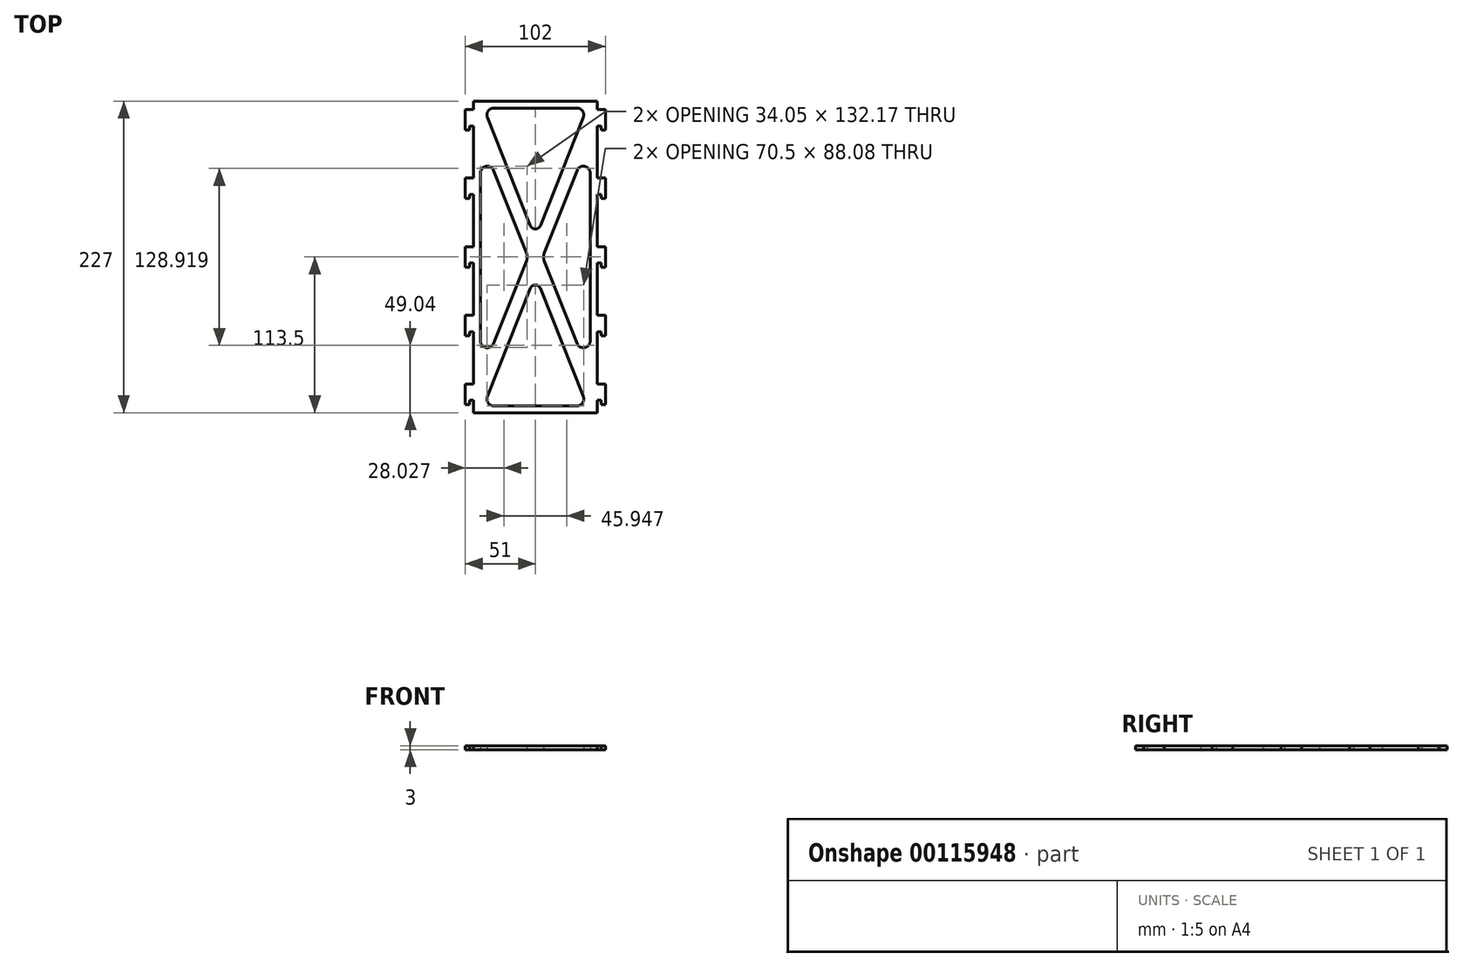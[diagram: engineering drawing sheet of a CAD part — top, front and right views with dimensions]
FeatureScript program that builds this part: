
annotation { "Feature Type Name" : "Feature", "Feature Type Description" : "" }
export const myFeature = defineFeature(function(context is Context, id is Id, definition is map)
    precondition{}
    {
        {
            var Q0;
            Q0=qCreatedBy(makeId("Top.planeOp"),FACE);
            var sketch = newSketch(context, id + "F0", { "sketchPlane" : qUnion([Q0])});
            skLineSegment(sketch, "E0.bottom", {"start": v(45, -113.5) * mm, "end": v(-45, -113.5) * mm});
            skLineSegment(sketch, "E0.top", {"start": v(45, 113.5) * mm, "end": v(-45, 113.5) * mm});
            skLineSegment(sketch, "E0.left", {"start": v(45, -113.5) * mm, "end": v(45, 113.5) * mm});
            skLineSegment(sketch, "E0.right", {"start": v(-45, -113.5) * mm, "end": v(-45, 113.5) * mm});
            skPoint(sketch, "E0.middle", {"position": v(0, 0) * mm});
            skLineSegment(sketch, "E1", {"start": v(-45, 113.5) * mm, "end": v(45, -113.5) * mm, "construction": true});
            skLineSegment(sketch, "E2", {"start": v(45, 113.5) * mm, "end": v(-45, -113.5) * mm, "construction": true});
            skLineSegment(sketch, "E3.0", {"start": v(-30.35, 62.99) * mm, "end": v(-6.47, 2.76) * mm});
            skLineSegment(sketch, "E4.0", {"start": v(-40, -61.15) * mm, "end": v(-40, 61.15) * mm});
            skLineSegment(sketch, "E5.0", {"start": v(-6.47, -2.76) * mm, "end": v(-30.35, -62.99) * mm});
            skArc(sketch, "E6.filletArc", {"start": v(-30.35, 62.99) * mm, "mid": v(-35.94, 66.06) * mm, "end": v(-40, 61.15) * mm});
            skArc(sketch, "E7.filletArc", {"start": v(-6.47, -2.76) * mm, "mid": v(-5.95, 0) * mm, "end": v(-6.47, 2.76) * mm});
            skArc(sketch, "E8.filletArc", {"start": v(-40, -61.15) * mm, "mid": v(-35.94, -66.06) * mm, "end": v(-30.35, -62.99) * mm});
            skLineSegment(sketch, "E9.0", {"start": v(34.93, 101.66) * mm, "end": v(3.72, 22.94) * mm});
            skLineSegment(sketch, "E10.0", {"start": v(-34.93, 101.66) * mm, "end": v(-3.72, 22.94) * mm});
            skLineSegment(sketch, "E11.0", {"start": v(30.28, 108.5) * mm, "end": v(-30.28, 108.5) * mm});
            skArc(sketch, "E12.filletArc", {"start": v(-30.28, 108.5) * mm, "mid": v(-34.41, 106.3) * mm, "end": v(-34.93, 101.66) * mm});
            skArc(sketch, "E13.filletArc", {"start": v(34.93, 101.66) * mm, "mid": v(34.41, 106.3) * mm, "end": v(30.28, 108.5) * mm});
            skArc(sketch, "E14.filletArc", {"start": v(-3.72, 22.94) * mm, "mid": v(0, 20.42) * mm, "end": v(3.72, 22.94) * mm});
            skLineSegment(sketch, "E15.MirrorCS", {"start": v(-34.93, -101.66) * mm, "end": v(-3.72, -22.94) * mm});
            skArc(sketch, "E16.MirrorCS", {"start": v(-30.28, -108.5) * mm, "mid": v(-34.41, -106.3) * mm, "end": v(-34.93, -101.66) * mm});
            skLineSegment(sketch, "E17.MirrorCS", {"start": v(30.28, -108.5) * mm, "end": v(-30.28, -108.5) * mm});
            skArc(sketch, "E18.MirrorCS", {"start": v(34.93, -101.66) * mm, "mid": v(34.41, -106.3) * mm, "end": v(30.28, -108.5) * mm});
            skLineSegment(sketch, "E19.MirrorCS", {"start": v(34.93, -101.66) * mm, "end": v(3.72, -22.94) * mm});
            skArc(sketch, "E20.MirrorCS", {"start": v(-3.72, -22.94) * mm, "mid": v(0, -20.42) * mm, "end": v(3.72, -22.94) * mm});
            skLineSegment(sketch, "E21.MirrorCS", {"start": v(30.35, 62.99) * mm, "end": v(6.47, 2.76) * mm});
            skArc(sketch, "E22.MirrorCS", {"start": v(30.35, 62.99) * mm, "mid": v(35.94, 66.06) * mm, "end": v(40, 61.15) * mm});
            skLineSegment(sketch, "E23.MirrorCS", {"start": v(40, -61.15) * mm, "end": v(40, 61.15) * mm});
            skArc(sketch, "E24.MirrorCS", {"start": v(40, -61.15) * mm, "mid": v(35.94, -66.06) * mm, "end": v(30.35, -62.99) * mm});
            skLineSegment(sketch, "E25.MirrorCS", {"start": v(6.47, -2.76) * mm, "end": v(30.35, -62.99) * mm});
            skArc(sketch, "E26.MirrorCS", {"start": v(6.47, -2.76) * mm, "mid": v(5.95, 0) * mm, "end": v(6.47, 2.76) * mm});
            skSolve(sketch);
        }
        {
            var Q0;
            Q0=makeQuery(id+"F0.imprint","IMPRINT",FACE,{"disambiguationData":[TD([[makeQuery(id+"F0.imprint","IMPRINT",EDGE,{"derivedFrom":sQuery(id+"F0.wireOp",EDGE,"E0.bottom")}),-1.0]])]});
            extrude(context, id + "F1", {"entities" : qUnion([Q0]), "depth" : 3 * mm});
        }
        {
            var Q0;
            Q0=makeQuery(id+"F1.opExtrude","CAP_FACE",FACE,{"disambiguationData":[OSD([sQuery(id+"F0.wireOp",EDGE,"E0.bottom"),sQuery(id+"F0.wireOp",EDGE,"E0.top"),sQuery(id+"F0.wireOp",EDGE,"E0.left"),sQuery(id+"F0.wireOp",EDGE,"E0.right"),sQuery(id+"F0.wireOp",EDGE,"E3.0"),sQuery(id+"F0.wireOp",EDGE,"E4.0"),sQuery(id+"F0.wireOp",EDGE,"E5.0"),sQuery(id+"F0.wireOp",EDGE,"E6.filletArc"),sQuery(id+"F0.wireOp",EDGE,"E7.filletArc"),sQuery(id+"F0.wireOp",EDGE,"E8.filletArc"),sQuery(id+"F0.wireOp",EDGE,"E9.0"),sQuery(id+"F0.wireOp",EDGE,"E10.0"),sQuery(id+"F0.wireOp",EDGE,"E11.0"),sQuery(id+"F0.wireOp",EDGE,"E12.filletArc"),sQuery(id+"F0.wireOp",EDGE,"E13.filletArc"),sQuery(id+"F0.wireOp",EDGE,"E14.filletArc"),sQuery(id+"F0.wireOp",EDGE,"E15.MirrorCS"),sQuery(id+"F0.wireOp",EDGE,"E16.MirrorCS"),sQuery(id+"F0.wireOp",EDGE,"E17.MirrorCS"),sQuery(id+"F0.wireOp",EDGE,"E18.MirrorCS"),sQuery(id+"F0.wireOp",EDGE,"E19.MirrorCS"),sQuery(id+"F0.wireOp",EDGE,"E20.MirrorCS"),sQuery(id+"F0.wireOp",EDGE,"E21.MirrorCS"),sQuery(id+"F0.wireOp",EDGE,"E22.MirrorCS"),sQuery(id+"F0.wireOp",EDGE,"E23.MirrorCS"),sQuery(id+"F0.wireOp",EDGE,"E24.MirrorCS"),sQuery(id+"F0.wireOp",EDGE,"E25.MirrorCS"),sQuery(id+"F0.wireOp",EDGE,"E26.MirrorCS")])],"isStart":false});
            var sketch = newSketch(context, id + "F2", { "sketchPlane" : qUnion([Q0])});
            skLineSegment(sketch, "E27.bottom", {"start": v(-45, 107.5) * mm, "end": v(-51, 107.5) * mm});
            skLineSegment(sketch, "E27.top", {"start": v(-48, 92.5) * mm, "end": v(-51, 92.5) * mm});
            skLineSegment(sketch, "E27.left", {"start": v(-45, 107.5) * mm, "end": v(-45, 95.5) * mm});
            skLineSegment(sketch, "E27.right", {"start": v(-51, 107.5) * mm, "end": v(-51, 92.5) * mm});
            skLineSegment(sketch, "E28.bottom", {"start": v(-45, 95.5) * mm, "end": v(-48, 95.5) * mm});
            skLineSegment(sketch, "E28.right", {"start": v(-48, 95.5) * mm, "end": v(-48, 92.5) * mm});
            skPoint(sketch, "E29.orphan", {"position": v(-45, 92.5) * mm});
            skLineSegment(sketch, "E30.MirrorCS", {"start": v(48, 92.5) * mm, "end": v(51, 92.5) * mm});
            skLineSegment(sketch, "E31.MirrorCS", {"start": v(48, 95.5) * mm, "end": v(48, 92.5) * mm});
            skLineSegment(sketch, "E32.MirrorCS", {"start": v(45, 95.5) * mm, "end": v(48, 95.5) * mm});
            skLineSegment(sketch, "E33.MirrorCS", {"start": v(51, 107.5) * mm, "end": v(51, 92.5) * mm});
            skLineSegment(sketch, "E34.MirrorCS", {"start": v(45, 107.5) * mm, "end": v(51, 107.5) * mm});
            skPoint(sketch, "E35.MirrorP", {"position": v(45, 92.5) * mm});
            skLineSegment(sketch, "E36.MirrorCS", {"start": v(45, 107.5) * mm, "end": v(45, 95.5) * mm});
            skLineSegment(sketch, "E37.0.1.0", {"start": v(-45, 57.5) * mm, "end": v(-51, 57.5) * mm});
            skLineSegment(sketch, "E37.0.1.1", {"start": v(45, 57.5) * mm, "end": v(45, 45.5) * mm});
            skPoint(sketch, "E37.0.1.2", {"position": v(45, 42.5) * mm});
            skLineSegment(sketch, "E37.0.1.3", {"start": v(51, 57.5) * mm, "end": v(51, 42.5) * mm});
            skLineSegment(sketch, "E37.0.1.4", {"start": v(45, 57.5) * mm, "end": v(51, 57.5) * mm});
            skLineSegment(sketch, "E37.0.1.5", {"start": v(-45, 57.5) * mm, "end": v(-45, 45.5) * mm});
            skLineSegment(sketch, "E37.0.1.6", {"start": v(-51, 57.5) * mm, "end": v(-51, 42.5) * mm});
            skPoint(sketch, "E37.0.1.7", {"position": v(-45, 42.5) * mm});
            skLineSegment(sketch, "E37.0.1.8", {"start": v(-48, 42.5) * mm, "end": v(-51, 42.5) * mm});
            skLineSegment(sketch, "E37.0.1.9", {"start": v(-45, 45.5) * mm, "end": v(-48, 45.5) * mm});
            skLineSegment(sketch, "E37.0.1.10", {"start": v(48, 42.5) * mm, "end": v(51, 42.5) * mm});
            skLineSegment(sketch, "E37.0.1.11", {"start": v(-48, 45.5) * mm, "end": v(-48, 42.5) * mm});
            skLineSegment(sketch, "E37.0.1.12", {"start": v(45, 45.5) * mm, "end": v(48, 45.5) * mm});
            skLineSegment(sketch, "E37.0.1.13", {"start": v(48, 45.5) * mm, "end": v(48, 42.5) * mm});
            skLineSegment(sketch, "E37.0.2.0", {"start": v(-45, 7.5) * mm, "end": v(-51, 7.5) * mm});
            skLineSegment(sketch, "E37.0.2.1", {"start": v(45, 7.5) * mm, "end": v(45, -4.5) * mm});
            skPoint(sketch, "E37.0.2.2", {"position": v(45, -7.5) * mm});
            skLineSegment(sketch, "E37.0.2.3", {"start": v(51, 7.5) * mm, "end": v(51, -7.5) * mm});
            skLineSegment(sketch, "E37.0.2.4", {"start": v(45, 7.5) * mm, "end": v(51, 7.5) * mm});
            skLineSegment(sketch, "E37.0.2.5", {"start": v(-45, 7.5) * mm, "end": v(-45, -4.5) * mm});
            skLineSegment(sketch, "E37.0.2.6", {"start": v(-51, 7.5) * mm, "end": v(-51, -7.5) * mm});
            skPoint(sketch, "E37.0.2.7", {"position": v(-45, -7.5) * mm});
            skLineSegment(sketch, "E37.0.2.8", {"start": v(-48, -7.5) * mm, "end": v(-51, -7.5) * mm});
            skLineSegment(sketch, "E37.0.2.9", {"start": v(-45, -4.5) * mm, "end": v(-48, -4.5) * mm});
            skLineSegment(sketch, "E37.0.2.10", {"start": v(48, -7.5) * mm, "end": v(51, -7.5) * mm});
            skLineSegment(sketch, "E37.0.2.11", {"start": v(-48, -4.5) * mm, "end": v(-48, -7.5) * mm});
            skLineSegment(sketch, "E37.0.2.12", {"start": v(45, -4.5) * mm, "end": v(48, -4.5) * mm});
            skLineSegment(sketch, "E37.0.2.13", {"start": v(48, -4.5) * mm, "end": v(48, -7.5) * mm});
            skLineSegment(sketch, "E37.0.3.0", {"start": v(-45, -42.5) * mm, "end": v(-51, -42.5) * mm});
            skLineSegment(sketch, "E37.0.3.1", {"start": v(45, -42.5) * mm, "end": v(45, -54.5) * mm});
            skPoint(sketch, "E37.0.3.2", {"position": v(45, -57.5) * mm});
            skLineSegment(sketch, "E37.0.3.3", {"start": v(51, -42.5) * mm, "end": v(51, -57.5) * mm});
            skLineSegment(sketch, "E37.0.3.4", {"start": v(45, -42.5) * mm, "end": v(51, -42.5) * mm});
            skLineSegment(sketch, "E37.0.3.5", {"start": v(-45, -42.5) * mm, "end": v(-45, -54.5) * mm});
            skLineSegment(sketch, "E37.0.3.6", {"start": v(-51, -42.5) * mm, "end": v(-51, -57.5) * mm});
            skPoint(sketch, "E37.0.3.7", {"position": v(-45, -57.5) * mm});
            skLineSegment(sketch, "E37.0.3.8", {"start": v(-48, -57.5) * mm, "end": v(-51, -57.5) * mm});
            skLineSegment(sketch, "E37.0.3.9", {"start": v(-45, -54.5) * mm, "end": v(-48, -54.5) * mm});
            skLineSegment(sketch, "E37.0.3.10", {"start": v(48, -57.5) * mm, "end": v(51, -57.5) * mm});
            skLineSegment(sketch, "E37.0.3.11", {"start": v(-48, -54.5) * mm, "end": v(-48, -57.5) * mm});
            skLineSegment(sketch, "E37.0.3.12", {"start": v(45, -54.5) * mm, "end": v(48, -54.5) * mm});
            skLineSegment(sketch, "E37.0.3.13", {"start": v(48, -54.5) * mm, "end": v(48, -57.5) * mm});
            skLineSegment(sketch, "E37.0.4.0", {"start": v(-45, -92.5) * mm, "end": v(-51, -92.5) * mm});
            skLineSegment(sketch, "E37.0.4.1", {"start": v(45, -92.5) * mm, "end": v(45, -104.5) * mm});
            skPoint(sketch, "E37.0.4.2", {"position": v(45, -107.5) * mm});
            skLineSegment(sketch, "E37.0.4.3", {"start": v(51, -92.5) * mm, "end": v(51, -107.5) * mm});
            skLineSegment(sketch, "E37.0.4.4", {"start": v(45, -92.5) * mm, "end": v(51, -92.5) * mm});
            skLineSegment(sketch, "E37.0.4.5", {"start": v(-45, -92.5) * mm, "end": v(-45, -104.5) * mm});
            skLineSegment(sketch, "E37.0.4.6", {"start": v(-51, -92.5) * mm, "end": v(-51, -107.5) * mm});
            skPoint(sketch, "E37.0.4.7", {"position": v(-45, -107.5) * mm});
            skLineSegment(sketch, "E37.0.4.8", {"start": v(-48, -107.5) * mm, "end": v(-51, -107.5) * mm});
            skLineSegment(sketch, "E37.0.4.9", {"start": v(-45, -104.5) * mm, "end": v(-48, -104.5) * mm});
            skLineSegment(sketch, "E37.0.4.10", {"start": v(48, -107.5) * mm, "end": v(51, -107.5) * mm});
            skLineSegment(sketch, "E37.0.4.11", {"start": v(-48, -104.5) * mm, "end": v(-48, -107.5) * mm});
            skLineSegment(sketch, "E37.0.4.12", {"start": v(45, -104.5) * mm, "end": v(48, -104.5) * mm});
            skLineSegment(sketch, "E37.0.4.13", {"start": v(48, -104.5) * mm, "end": v(48, -107.5) * mm});
            skLineSegment(sketch, "E37.direction1", {"start": v(-51, 92.5) * mm, "end": v(-26, 92.5) * mm, "construction": true});
            skLineSegment(sketch, "E37.direction2", {"start": v(-51, 92.5) * mm, "end": v(-51, 42.5) * mm, "construction": true});
            skSolve(sketch);
        }
        {
            var Q0;
            Q0=makeQuery(id+"F2.imprint","IMPRINT",FACE,{"disambiguationData":[TD([[makeQuery(id+"F2.imprint","IMPRINT",EDGE,{"derivedFrom":sQuery(id+"F2.wireOp",EDGE,"E27.bottom")}),1.0]])]});
            var Q1;
            Q1=makeQuery(id+"F2.imprint","IMPRINT",FACE,{"disambiguationData":[TD([[makeQuery(id+"F2.imprint","IMPRINT",EDGE,{"derivedFrom":sQuery(id+"F2.wireOp",EDGE,"E30.MirrorCS")}),1.0]])]});
            var Q2;
            Q2=makeQuery(id+"F2.imprint","IMPRINT",FACE,{"disambiguationData":[TD([[makeQuery(id+"F2.imprint","IMPRINT",EDGE,{"derivedFrom":sQuery(id+"F2.wireOp",EDGE,"10417a5b-532b-4976-862d-c60a73cd2f560.MirrorCS")}),1.0]])]});
            var Q3;
            Q3=makeQuery(id+"F2.imprint","IMPRINT",FACE,{"disambiguationData":[TD([[makeQuery(id+"F2.imprint","IMPRINT",EDGE,{"derivedFrom":sQuery(id+"F2.wireOp",EDGE,"ZwzOGsWh-Hm2y-Uj7Z-gIu2-B6aL8R7svaD3.bottom")}),-1.0]])]});
            var Q4;
            Q4=makeQuery(id+"F2.imprint","IMPRINT",FACE,{"disambiguationData":[TD([[makeQuery(id+"F2.imprint","IMPRINT",EDGE,{"derivedFrom":sQuery(id+"F2.wireOp",EDGE,"E37.0.1.0")}),1.0]])]});
            var Q5;
            Q5=makeQuery(id+"F2.imprint","IMPRINT",FACE,{"disambiguationData":[TD([[makeQuery(id+"F2.imprint","IMPRINT",EDGE,{"derivedFrom":sQuery(id+"F2.wireOp",EDGE,"E37.0.1.1")}),-1.0]])]});
            var Q6;
            {var subQ0=sQuery(id+"F2.wireOp",EDGE,"E27.left");Q6=makeQuery(id+"F2.imprint","IMPRINT",FACE,{"disambiguationData":[TD([[makeQuery(id+"F2.imprint","IMPRINT",EDGE,{"derivedFrom":subQ0}),-1.0]])]});}
            var Q7;
            Q7=makeQuery(id+"F2.imprint","IMPRINT",FACE,{"disambiguationData":[TD([[makeQuery(id+"F2.imprint","IMPRINT",EDGE,{"derivedFrom":sQuery(id+"F2.wireOp",EDGE,"E37.0.2.0")}),1.0]])]});
            var Q8;
            Q8=makeQuery(id+"F2.imprint","IMPRINT",FACE,{"disambiguationData":[TD([[makeQuery(id+"F2.imprint","IMPRINT",EDGE,{"derivedFrom":sQuery(id+"F2.wireOp",EDGE,"E37.0.3.0")}),1.0]])]});
            var Q9;
            Q9=makeQuery(id+"F2.imprint","IMPRINT",FACE,{"disambiguationData":[TD([[makeQuery(id+"F2.imprint","IMPRINT",EDGE,{"derivedFrom":sQuery(id+"F2.wireOp",EDGE,"E37.0.4.0")}),1.0]])]});
            var Q10;
            Q10=makeQuery(id+"F2.imprint","IMPRINT",FACE,{"disambiguationData":[TD([[makeQuery(id+"F2.imprint","IMPRINT",EDGE,{"derivedFrom":sQuery(id+"F2.wireOp",EDGE,"E37.0.4.1")}),-1.0]])]});
            var Q11;
            Q11=makeQuery(id+"F2.imprint","IMPRINT",FACE,{"disambiguationData":[TD([[makeQuery(id+"F2.imprint","IMPRINT",EDGE,{"derivedFrom":sQuery(id+"F2.wireOp",EDGE,"E37.0.3.1")}),-1.0]])]});
            var Q12;
            Q12=makeQuery(id+"F2.imprint","IMPRINT",FACE,{"disambiguationData":[TD([[makeQuery(id+"F2.imprint","IMPRINT",EDGE,{"derivedFrom":sQuery(id+"F2.wireOp",EDGE,"E37.0.2.1")}),-1.0]])]});
            var Q13;
            Q13=makeQuery(id+"F1.opExtrude","CAP_FACE",FACE,{"disambiguationData":[OSD([sQuery(id+"F0.wireOp",EDGE,"E0.bottom"),sQuery(id+"F0.wireOp",EDGE,"E0.top"),sQuery(id+"F0.wireOp",EDGE,"E0.left"),sQuery(id+"F0.wireOp",EDGE,"E0.right"),sQuery(id+"F0.wireOp",EDGE,"E3.0"),sQuery(id+"F0.wireOp",EDGE,"E4.0"),sQuery(id+"F0.wireOp",EDGE,"E5.0"),sQuery(id+"F0.wireOp",EDGE,"E6.filletArc"),sQuery(id+"F0.wireOp",EDGE,"E7.filletArc"),sQuery(id+"F0.wireOp",EDGE,"E8.filletArc"),sQuery(id+"F0.wireOp",EDGE,"E9.0"),sQuery(id+"F0.wireOp",EDGE,"E10.0"),sQuery(id+"F0.wireOp",EDGE,"E11.0"),sQuery(id+"F0.wireOp",EDGE,"E12.filletArc"),sQuery(id+"F0.wireOp",EDGE,"E13.filletArc"),sQuery(id+"F0.wireOp",EDGE,"E14.filletArc"),sQuery(id+"F0.wireOp",EDGE,"E15.MirrorCS"),sQuery(id+"F0.wireOp",EDGE,"E16.MirrorCS"),sQuery(id+"F0.wireOp",EDGE,"E17.MirrorCS"),sQuery(id+"F0.wireOp",EDGE,"E18.MirrorCS"),sQuery(id+"F0.wireOp",EDGE,"E19.MirrorCS"),sQuery(id+"F0.wireOp",EDGE,"E20.MirrorCS"),sQuery(id+"F0.wireOp",EDGE,"E21.MirrorCS"),sQuery(id+"F0.wireOp",EDGE,"E22.MirrorCS"),sQuery(id+"F0.wireOp",EDGE,"E23.MirrorCS"),sQuery(id+"F0.wireOp",EDGE,"E24.MirrorCS"),sQuery(id+"F0.wireOp",EDGE,"E25.MirrorCS"),sQuery(id+"F0.wireOp",EDGE,"E26.MirrorCS")])],"isStart":true});
            extrude(context, id + "F3", {"entities" : qUnion([Q0, Q1, Q2, Q3, Q4, Q5, Q6, Q7, Q8, Q9, Q10, Q11, Q12]), "operationType" : NewBodyOperationType.ADD, "endBound" : BoundingType.UP_TO_SURFACE, "oppositeDirection" : true, "endBoundEntityFace" : qUnion([Q13]), "depth" : 25 * mm});
        }
    });
